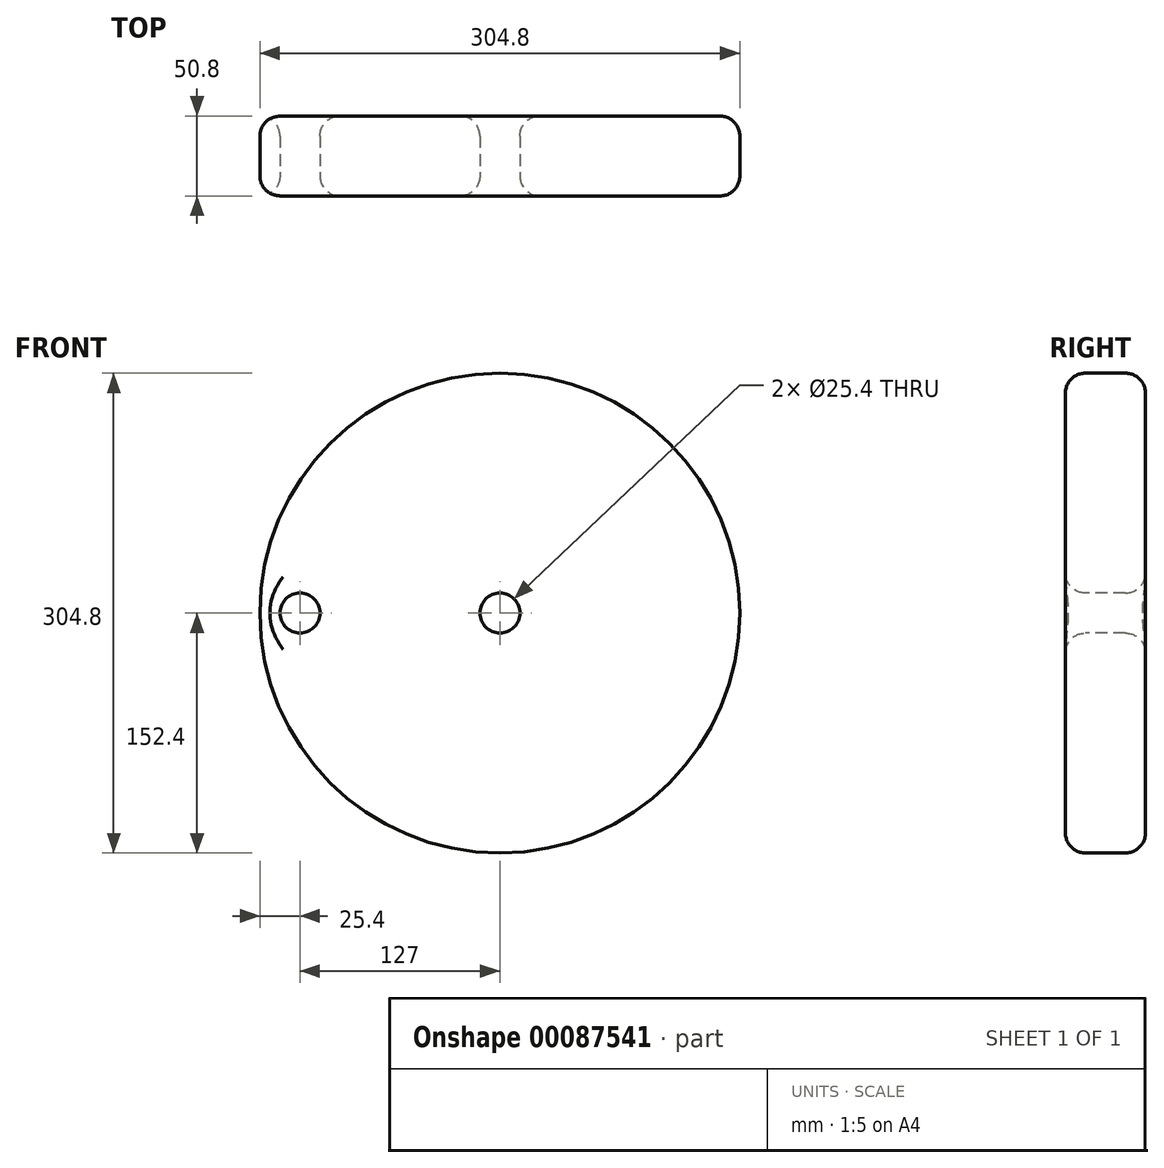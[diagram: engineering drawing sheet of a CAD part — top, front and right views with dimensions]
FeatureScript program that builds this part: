
annotation { "Feature Type Name" : "Feature", "Feature Type Description" : "" }
export const myFeature = defineFeature(function(context is Context, id is Id, definition is map)
    precondition{}
    {
        {
            var Q0;
            Q0=qCreatedBy(makeId("Front.planeOp"),FACE);
            var sketch = newSketch(context, id + "F0", { "sketchPlane" : qUnion([Q0])});
            skCircle(sketch, "E0", {"center": v(0, 0) * mm, "radius": 152.4 * mm});
            skSolve(sketch);
        }
        {
            var Q0;
            Q0=makeQuery(id+"F0.imprint","IMPRINT",FACE,{"disambiguationData":[TD([[makeQuery(id+"F0.imprint","IMPRINT",EDGE,{"derivedFrom":sQuery(id+"F0.wireOp",EDGE,"E0")}),1.0]])]});
            extrude(context, id + "F1", {"entities" : qUnion([Q0]), "depth" : 50.8 * mm});
        }
        {
            var Q0;
            Q0=makeQuery(id+"F1.opExtrude","CAP_FACE",FACE,{"disambiguationData":[OSD([sQuery(id+"F0.wireOp",EDGE,"E0")])],"isStart":false});
            var sketch = newSketch(context, id + "F2", { "sketchPlane" : qUnion([Q0])});
            skCircle(sketch, "E1", {"center": v(0, 0) * mm, "radius": 12.7 * mm});
            skCircle(sketch, "E2", {"center": v(0, 0) * mm, "radius": 127 * mm, "construction": true});
            skPoint(sketch, "E3.center.orphan", {"position": v(-75.47, 0) * mm});
            skCircle(sketch, "E4", {"center": v(-127, 0) * mm, "radius": 12.7 * mm});
            skSolve(sketch);
        }
        {
            var Q0;
            Q0 = qSketchRegion(id + "F2", true);
            extrude(context, id + "F3", {"entities" : qUnion([Q0]), "operationType" : NewBodyOperationType.REMOVE, "endBound" : BoundingType.THROUGH_ALL, "oppositeDirection" : true, "depth" : 25.4 * mm});
        }
        {
            var Q0;
            Q0=makeQuery(id+"F1.opExtrude","CAP_FACE",FACE,{"disambiguationData":[OSD([sQuery(id+"F0.wireOp",EDGE,"E0")])],"isStart":false});
            var Q1;
            Q1=makeQuery(id+"F1.opExtrude","CAP_FACE",FACE,{"disambiguationData":[OSD([sQuery(id+"F0.wireOp",EDGE,"E0")])],"isStart":true});
            fillet(context, id + "F4", {"entities" : qUnion([Q0, Q1]), "radius" : 12.7 * mm, "tangentPropagation" : true, "allowEdgeOverflow" : false});
        }
    });
